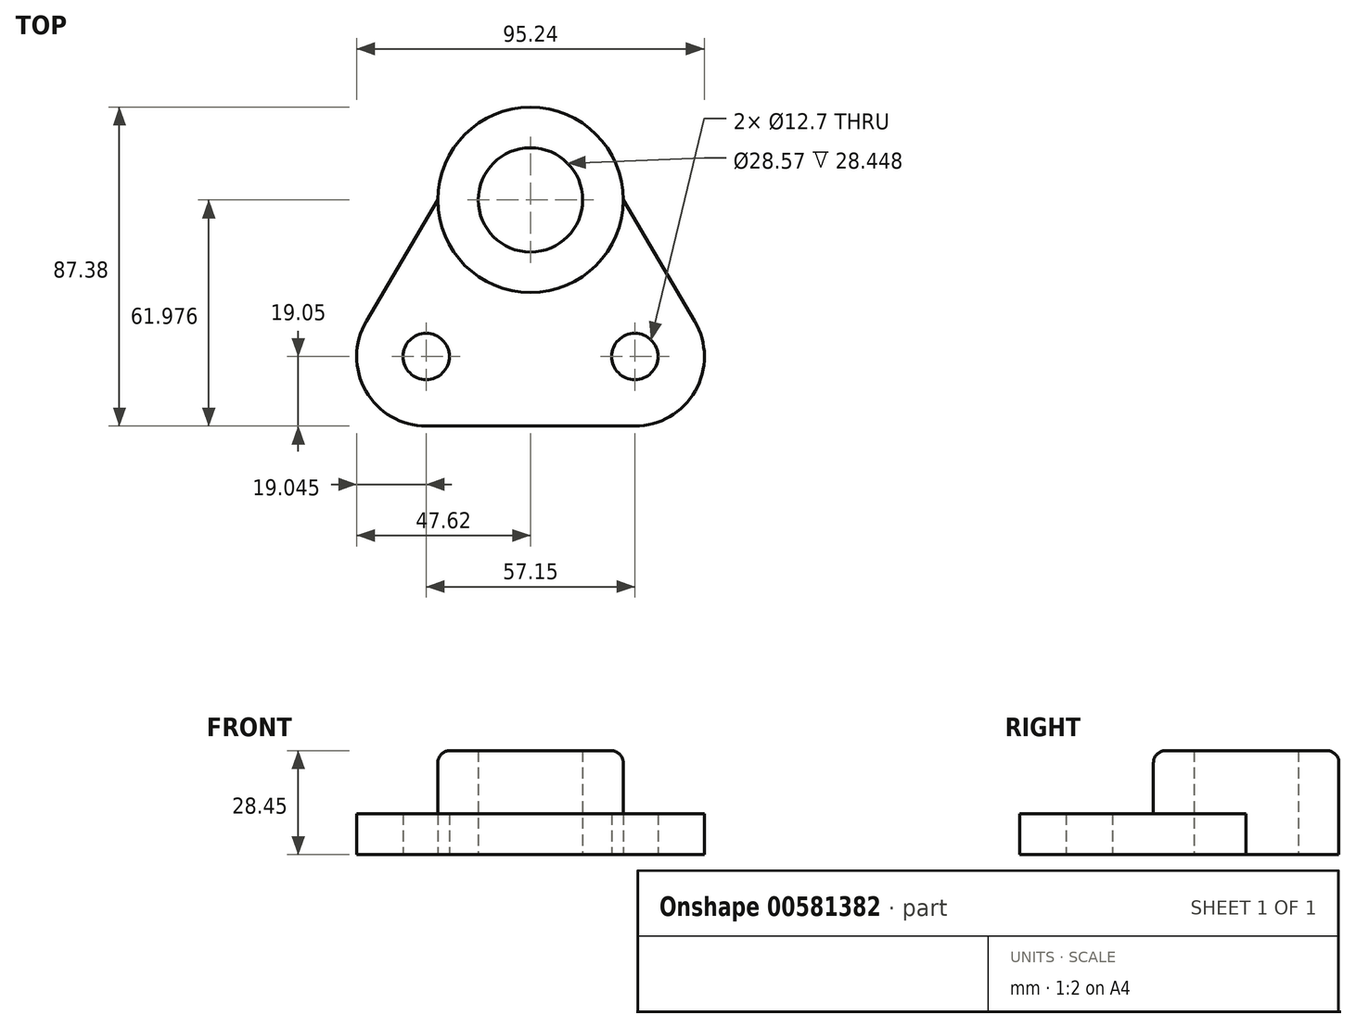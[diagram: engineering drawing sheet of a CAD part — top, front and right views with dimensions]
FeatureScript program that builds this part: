
annotation { "Feature Type Name" : "Feature", "Feature Type Description" : "" }
export const myFeature = defineFeature(function(context is Context, id is Id, definition is map)
    precondition{}
    {
        {
            var Q0;
            Q0=qCreatedBy(makeId("Top.planeOp"),FACE);
            var sketch = newSketch(context, id + "F0", { "sketchPlane" : qUnion([Q0])});
            skLineSegment(sketch, "E0", {"start": v(0, 0) * mm, "end": v(-28.57, 0) * mm});
            skLineSegment(sketch, "E1.MirrorCS", {"start": v(0, 0) * mm, "end": v(28.57, 0) * mm});
            skCircle(sketch, "E2", {"center": v(0, 61.98) * mm, "radius": 14.29 * mm});
            skCircle(sketch, "E3", {"center": v(0, 61.98) * mm, "radius": 25.4 * mm});
            skArc(sketch, "E4", {"start": v(-44.99, 28.72) * mm, "mid": v(-45.11, 9.6) * mm, "end": v(-28.58, 0) * mm});
            skArc(sketch, "E5.MirrorCS", {"start": v(44.99, 28.72) * mm, "mid": v(45.11, 9.6) * mm, "end": v(28.58, 0) * mm});
            skLineSegment(sketch, "E6", {"start": v(-25.4, 61.98) * mm, "end": v(-44.99, 28.72) * mm});
            skLineSegment(sketch, "E7", {"start": v(25.4, 61.98) * mm, "end": v(44.99, 28.72) * mm});
            skCircle(sketch, "E8", {"center": v(-28.58, 19.05) * mm, "radius": 6.35 * mm});
            skCircle(sketch, "E9", {"center": v(28.58, 19.05) * mm, "radius": 6.35 * mm});
            skSolve(sketch);
        }
        {
            var Q0;
            Q0=makeQuery(id+"F0.imprint","IMPRINT",FACE,{"disambiguationData":[TD([[makeQuery(id+"F0.imprint","IMPRINT",EDGE,{"derivedFrom":sQuery(id+"F0.wireOp",EDGE,"E2")}),-1.0]])]});
            extrude(context, id + "F1", {"entities" : qUnion([Q0]), "depth" : 28.45 * mm, "offsetDistance" : 25.4 * mm});
        }
        {
            var Q0;
            Q0=makeQuery(id+"F0.imprint","IMPRINT",FACE,{"disambiguationData":[TD([[makeQuery(id+"F0.imprint","IMPRINT",EDGE,{"derivedFrom":sQuery(id+"F0.wireOp",EDGE,"E0")}),-1.0]])]});
            extrude(context, id + "F2", {"entities" : qUnion([Q0]), "operationType" : NewBodyOperationType.ADD, "depth" : 11.18 * mm, "offsetDistance" : 25.4 * mm});
        }
        {
            var Q0;
            Q0=makeQuery(id+"F1.opExtrude","CAP_EDGE",EDGE,{"disambiguationData":[OSD([sQuery(id+"F0.wireOp",EDGE,"E3")])],"isStart":false});
            fillet(context, id + "F3", {"entities" : qUnion([Q0]), "radius" : 3.3 * mm, "tangentPropagation" : true, "allowEdgeOverflow" : false});
        }
    });
